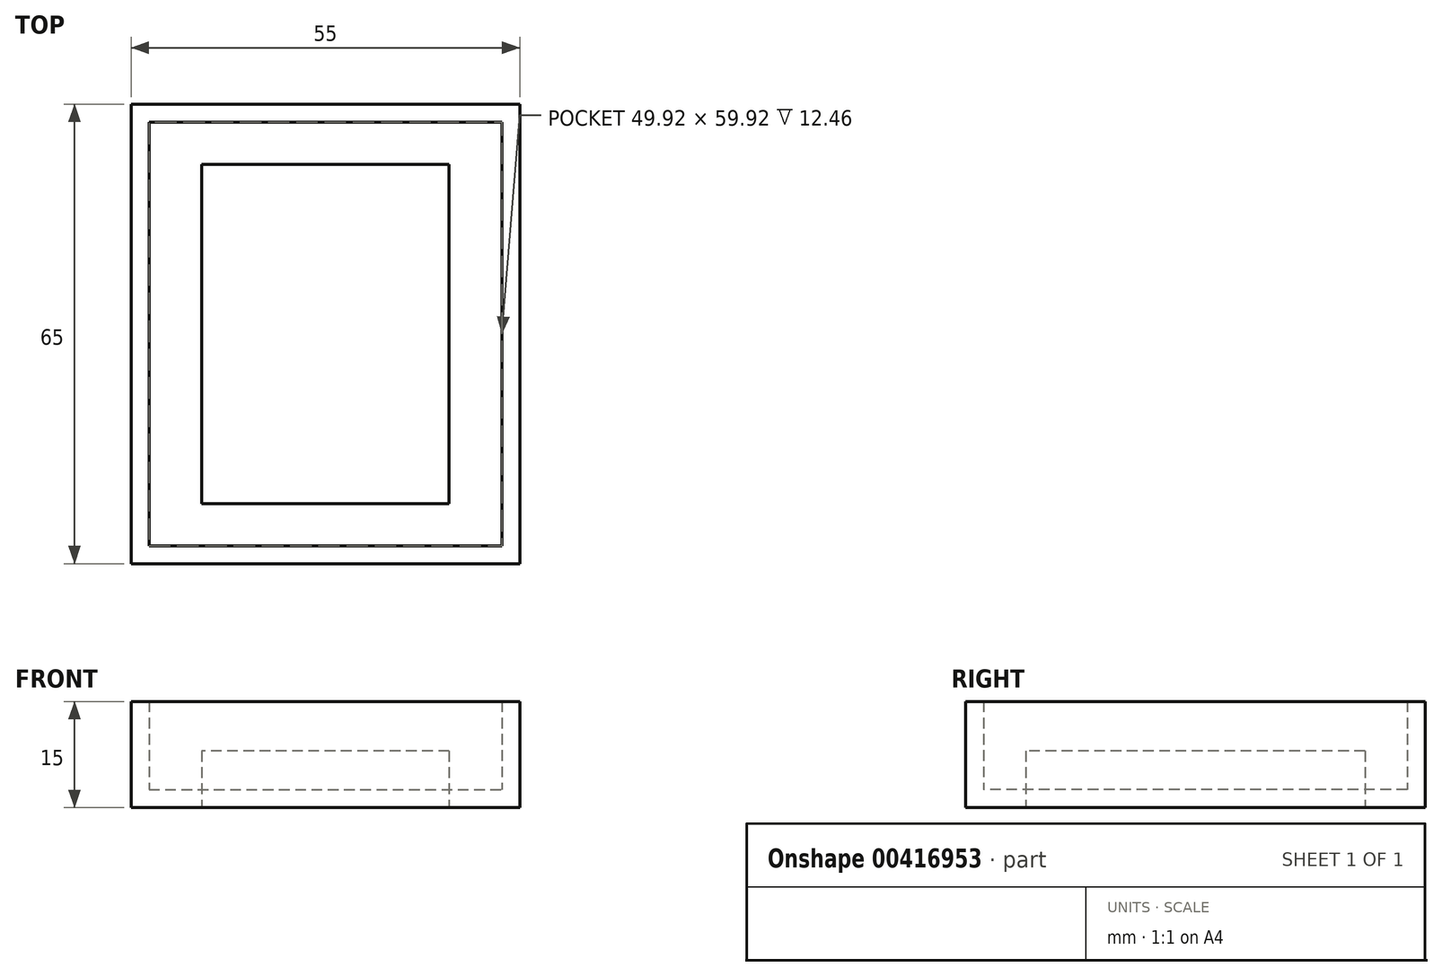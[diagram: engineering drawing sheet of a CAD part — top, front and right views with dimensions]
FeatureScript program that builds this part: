
annotation { "Feature Type Name" : "Feature", "Feature Type Description" : "" }
export const myFeature = defineFeature(function(context is Context, id is Id, definition is map)
    precondition{}
    {
        {
            var Q0;
            Q0=qCreatedBy(makeId("Top.planeOp"),FACE);
            var sketch = newSketch(context, id + "F0", { "sketchPlane" : qUnion([Q0])});
            skLineSegment(sketch, "E0.bottom", {"start": v(-27.5, 32.5) * mm, "end": v(27.5, 32.5) * mm});
            skLineSegment(sketch, "E0.top", {"start": v(-27.5, -32.5) * mm, "end": v(27.5, -32.5) * mm});
            skLineSegment(sketch, "E0.left", {"start": v(-27.5, 32.5) * mm, "end": v(-27.5, -32.5) * mm});
            skLineSegment(sketch, "E0.right", {"start": v(27.5, 32.5) * mm, "end": v(27.5, -32.5) * mm});
            skPoint(sketch, "E1", {"position": v(0, 32.5) * mm});
            skPoint(sketch, "E2", {"position": v(27.5, 0) * mm});
            skSolve(sketch);
        }
        {
            var Q0;
            Q0=makeQuery(id+"F0.imprint","IMPRINT",FACE,{"disambiguationData":[TD([[makeQuery(id+"F0.imprint","IMPRINT",EDGE,{"derivedFrom":sQuery(id+"F0.wireOp",EDGE,"E0.bottom")}),-1.0]])]});
            extrude(context, id + "F1", {"entities" : qUnion([Q0]), "depth" : 15 * mm});
        }
        {
            var Q0;
            Q0=makeQuery(id+"F1.opExtrude","CAP_FACE",FACE,{"disambiguationData":[OSD([sQuery(id+"F0.wireOp",EDGE,"E0.bottom"),sQuery(id+"F0.wireOp",EDGE,"E0.top"),sQuery(id+"F0.wireOp",EDGE,"E0.left"),sQuery(id+"F0.wireOp",EDGE,"E0.right")])],"isStart":false});
            shell(context, id + "F2", {"entities" : qUnion([Q0]), "thickness" : 2.54 * mm});
        }
        {
            var Q0;
            Q0=qCreatedBy(makeId("Top.planeOp"),FACE);
            var sketch = newSketch(context, id + "F3", { "sketchPlane" : qUnion([Q0])});
            skLineSegment(sketch, "E3.bottom", {"start": v(17.5, 24) * mm, "end": v(-17.5, 24) * mm});
            skLineSegment(sketch, "E3.top", {"start": v(17.5, -24) * mm, "end": v(-17.5, -24) * mm});
            skLineSegment(sketch, "E3.left", {"start": v(17.5, 24) * mm, "end": v(17.5, -24) * mm});
            skLineSegment(sketch, "E3.right", {"start": v(-17.5, 24) * mm, "end": v(-17.5, -24) * mm});
            skPoint(sketch, "E4", {"position": v(17.5, 0) * mm});
            skPoint(sketch, "E5", {"position": v(0, -24) * mm});
            skSolve(sketch);
        }
        {
            var Q0;
            Q0=makeQuery(id+"F3.imprint","IMPRINT",FACE,{"disambiguationData":[TD([[makeQuery(id+"F3.imprint","IMPRINT",EDGE,{"derivedFrom":sQuery(id+"F3.wireOp",EDGE,"E3.bottom")}),1.0]])]});
            extrude(context, id + "F4", {"entities" : qUnion([Q0]), "depth" : 8 * mm});
        }
    });
